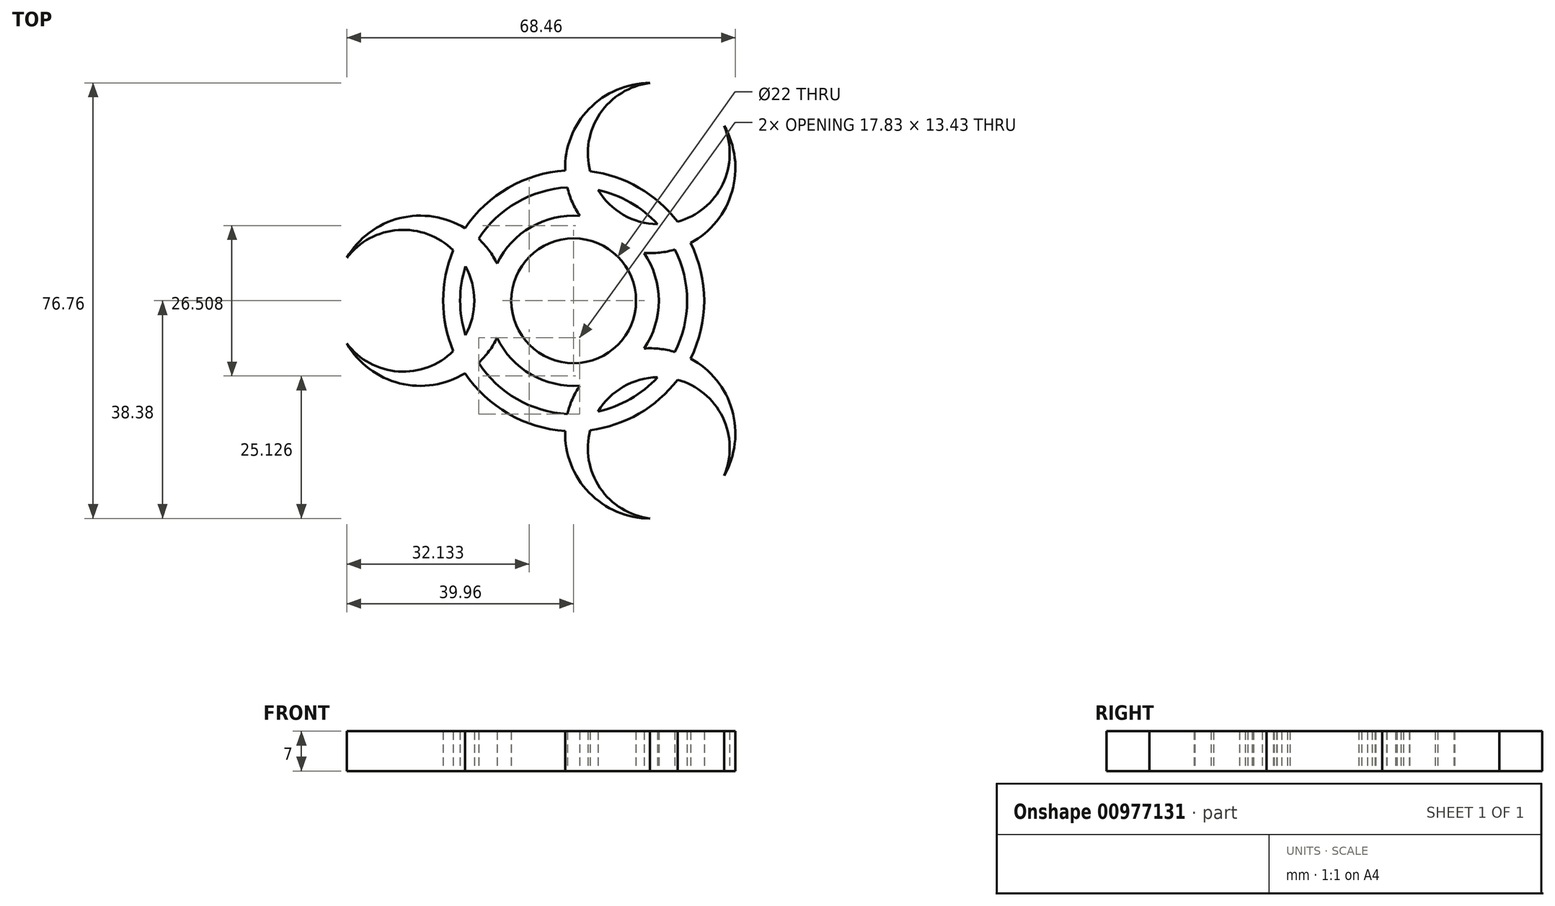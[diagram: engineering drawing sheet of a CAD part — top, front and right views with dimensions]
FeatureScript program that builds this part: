
annotation { "Feature Type Name" : "Feature", "Feature Type Description" : "" }
export const myFeature = defineFeature(function(context is Context, id is Id, definition is map)
    precondition{}
    {
        {
            var Q0;
            Q0=qCreatedBy(makeId("Top.planeOp"),FACE);
            var sketch = newSketch(context, id + "F0", { "sketchPlane" : qUnion([Q0])});
            skCircle(sketch, "E0", {"center": v(0, 0) * mm, "radius": 11 * mm});
            skCircle(sketch, "E1", {"center": v(0, 0) * mm, "radius": 15 * mm});
            skCircle(sketch, "E2", {"center": v(-27, 0) * mm, "radius": 15 * mm});
            skCircle(sketch, "E3", {"center": v(-30, 0) * mm, "radius": 12.5 * mm});
            skCircle(sketch, "E4", {"center": v(0, 0) * mm, "radius": 20 * mm});
            skCircle(sketch, "E5", {"center": v(0, 0) * mm, "radius": 23 * mm});
            skSolve(sketch);
        }
        {
            var Q0;
            {var subQ0=sQuery(id+"F0.wireOp",EDGE,"A1HAMbn4-FVia-Wbmo-pdO5-hsUaKxTLg120");var subQ1=sQuery(id+"F0.wireOp",EDGE,"E0");var subQ2=makeQuery(id+"F0.imprint","INTERSECT",VERTEX,{"disambiguationData":[OD(0.0)],"derivedFrom":[subQ1,subQ0]});Q0=makeQuery(id+"F0.imprint","IMPRINT",FACE,{"disambiguationData":[TD([[makeQuery(id+"F0.imprint","IMPRINT",EDGE,{"disambiguationData":[TD([[subQ2,-1.0]])],"derivedFrom":subQ1}),-1.0]])]});}
            var Q1;
            {var subQ0=sQuery(id+"F0.wireOp",EDGE,"E2");var subQ1=sQuery(id+"F0.wireOp",EDGE,"E1");var subQ2=makeQuery(id+"F0.imprint","INTERSECT",VERTEX,{"disambiguationData":[OD(0.0)],"derivedFrom":[subQ1,subQ0]});Q1=makeQuery(id+"F0.imprint","IMPRINT",FACE,{"disambiguationData":[TD([[makeQuery(id+"F0.imprint","IMPRINT",EDGE,{"disambiguationData":[TD([[subQ2,-1.0]])],"derivedFrom":subQ1}),-1.0]])]});}
            var Q2;
            {var subQ0=sQuery(id+"F0.wireOp",EDGE,"E2");var subQ1=sQuery(id+"F0.wireOp",EDGE,"E1");var subQ2=makeQuery(id+"F0.imprint","INTERSECT",VERTEX,{"disambiguationData":[OD(0.0)],"derivedFrom":[subQ1,subQ0]});Q2=makeQuery(id+"F0.imprint","IMPRINT",FACE,{"disambiguationData":[TD([[makeQuery(id+"F0.imprint","IMPRINT",EDGE,{"disambiguationData":[TD([[subQ2,-1.0]])],"derivedFrom":subQ1}),1.0]])]});}
            var Q3;
            {var subQ0=sQuery(id+"F0.wireOp",EDGE,"u9p2bbKC-iFeF-zK1N-2cqy-84KDiadLL0JS");var subQ1=sQuery(id+"F0.wireOp",EDGE,"E2");var subQ2=makeQuery(id+"F0.imprint","INTERSECT",VERTEX,{"disambiguationData":[OD(1.0)],"derivedFrom":[subQ1,subQ0]});Q3=makeQuery(id+"F0.imprint","IMPRINT",FACE,{"disambiguationData":[TD([[makeQuery(id+"F0.imprint","IMPRINT",EDGE,{"disambiguationData":[TD([[subQ2,-1.0]])],"derivedFrom":subQ1}),1.0]])]});}
            var Q4;
            {var subQ0=sQuery(id+"F0.wireOp",EDGE,"u9p2bbKC-iFeF-zK1N-2cqy-84KDiadLL0JS");var subQ1=sQuery(id+"F0.wireOp",EDGE,"E2");var subQ2=makeQuery(id+"F0.imprint","INTERSECT",VERTEX,{"disambiguationData":[OD(0.0)],"derivedFrom":[subQ1,subQ0]});Q4=makeQuery(id+"F0.imprint","IMPRINT",FACE,{"disambiguationData":[TD([[makeQuery(id+"F0.imprint","IMPRINT",EDGE,{"disambiguationData":[TD([[subQ2,1.0]])],"derivedFrom":subQ1}),-1.0]])]});}
            var Q5;
            {var subQ0=sQuery(id+"F0.wireOp",EDGE,"E5");var subQ1=sQuery(id+"F0.wireOp",EDGE,"E2");var subQ2=makeQuery(id+"F0.imprint","INTERSECT",VERTEX,{"disambiguationData":[OD(0.0)],"derivedFrom":[subQ1,subQ0]});Q5=makeQuery(id+"F0.imprint","IMPRINT",FACE,{"disambiguationData":[TD([[makeQuery(id+"F0.imprint","IMPRINT",EDGE,{"disambiguationData":[TD([[subQ2,-1.0]])],"derivedFrom":subQ1}),1.0]])]});}
            var Q6;
            {var subQ0=sQuery(id+"F0.wireOp",EDGE,"E5");var subQ1=sQuery(id+"F0.wireOp",EDGE,"E3");var subQ2=makeQuery(id+"F0.imprint","INTERSECT",VERTEX,{"disambiguationData":[OD(0.0)],"derivedFrom":[subQ1,subQ0]});Q6=makeQuery(id+"F0.imprint","IMPRINT",FACE,{"disambiguationData":[TD([[makeQuery(id+"F0.imprint","IMPRINT",EDGE,{"disambiguationData":[TD([[subQ2,1.0]])],"derivedFrom":subQ1}),1.0]])]});}
            var Q7;
            {var subQ0=sQuery(id+"F0.wireOp",EDGE,"E5");var subQ1=sQuery(id+"F0.wireOp",EDGE,"E2");var subQ2=makeQuery(id+"F0.imprint","INTERSECT",VERTEX,{"disambiguationData":[OD(0.0)],"derivedFrom":[subQ1,subQ0]});Q7=makeQuery(id+"F0.imprint","IMPRINT",FACE,{"disambiguationData":[TD([[makeQuery(id+"F0.imprint","IMPRINT",EDGE,{"disambiguationData":[TD([[subQ2,1.0]])],"derivedFrom":subQ1}),-1.0]])]});}
            var Q8;
            {var subQ0=sQuery(id+"F0.wireOp",EDGE,"E5");var subQ1=sQuery(id+"F0.wireOp",EDGE,"E2");var subQ2=makeQuery(id+"F0.imprint","INTERSECT",VERTEX,{"disambiguationData":[OD(1.0)],"derivedFrom":[subQ1,subQ0]});Q8=makeQuery(id+"F0.imprint","IMPRINT",FACE,{"disambiguationData":[TD([[makeQuery(id+"F0.imprint","IMPRINT",EDGE,{"disambiguationData":[TD([[subQ2,-1.0]])],"derivedFrom":subQ1}),1.0]])]});}
            var Q9;
            {var subQ0=sQuery(id+"F0.wireOp",EDGE,"E5");var subQ1=sQuery(id+"F0.wireOp",EDGE,"E2");var subQ2=makeQuery(id+"F0.imprint","INTERSECT",VERTEX,{"disambiguationData":[OD(0.0)],"derivedFrom":[subQ1,subQ0]});Q9=makeQuery(id+"F0.imprint","IMPRINT",FACE,{"disambiguationData":[TD([[makeQuery(id+"F0.imprint","IMPRINT",EDGE,{"disambiguationData":[TD([[subQ2,1.0]])],"derivedFrom":subQ1}),1.0]])]});}
            var Q10;
            {var subQ0=sQuery(id+"F0.wireOp",EDGE,"E3");var subQ1=sQuery(id+"F0.wireOp",EDGE,"E2");var subQ2=makeQuery(id+"F0.imprint","INTERSECT",VERTEX,{"disambiguationData":[OD(1.0)],"derivedFrom":[subQ1,subQ0]});Q10=makeQuery(id+"F0.imprint","IMPRINT",FACE,{"disambiguationData":[TD([[makeQuery(id+"F0.imprint","IMPRINT",EDGE,{"disambiguationData":[TD([[subQ2,-1.0]])],"derivedFrom":subQ1}),1.0]])]});}
            extrude(context, id + "F1", {"entities" : qUnion([Q0, Q1, Q2, Q3, Q4, Q5, Q6, Q7, Q8, Q9, Q10]), "depth" : 7 * mm, "offsetDistance" : 25 * mm});
        }
        {
            var Q0;
            Q0=makeQuery(id+"F1.opExtrude","SWEPT_BODY",BODY,{"disambiguationData":[OSD([sQuery(id+"F0.wireOp",EDGE,"E0"),sQuery(id+"F0.wireOp",EDGE,"E1"),sQuery(id+"F0.wireOp",EDGE,"E2"),sQuery(id+"F0.wireOp",EDGE,"E3")])]});
            var Q1;
            Q1=sQuery(id+"F0.wireOp",EDGE,"E0");
            circularPattern(context, id + "F2", {"operationType" : NewBodyOperationType.ADD, "entities" : qUnion([Q0]), "axis" : qUnion([Q1]), "angle" : 360 * degree, "instanceCount" : 3, "equalSpace" : true});
        }
    });
